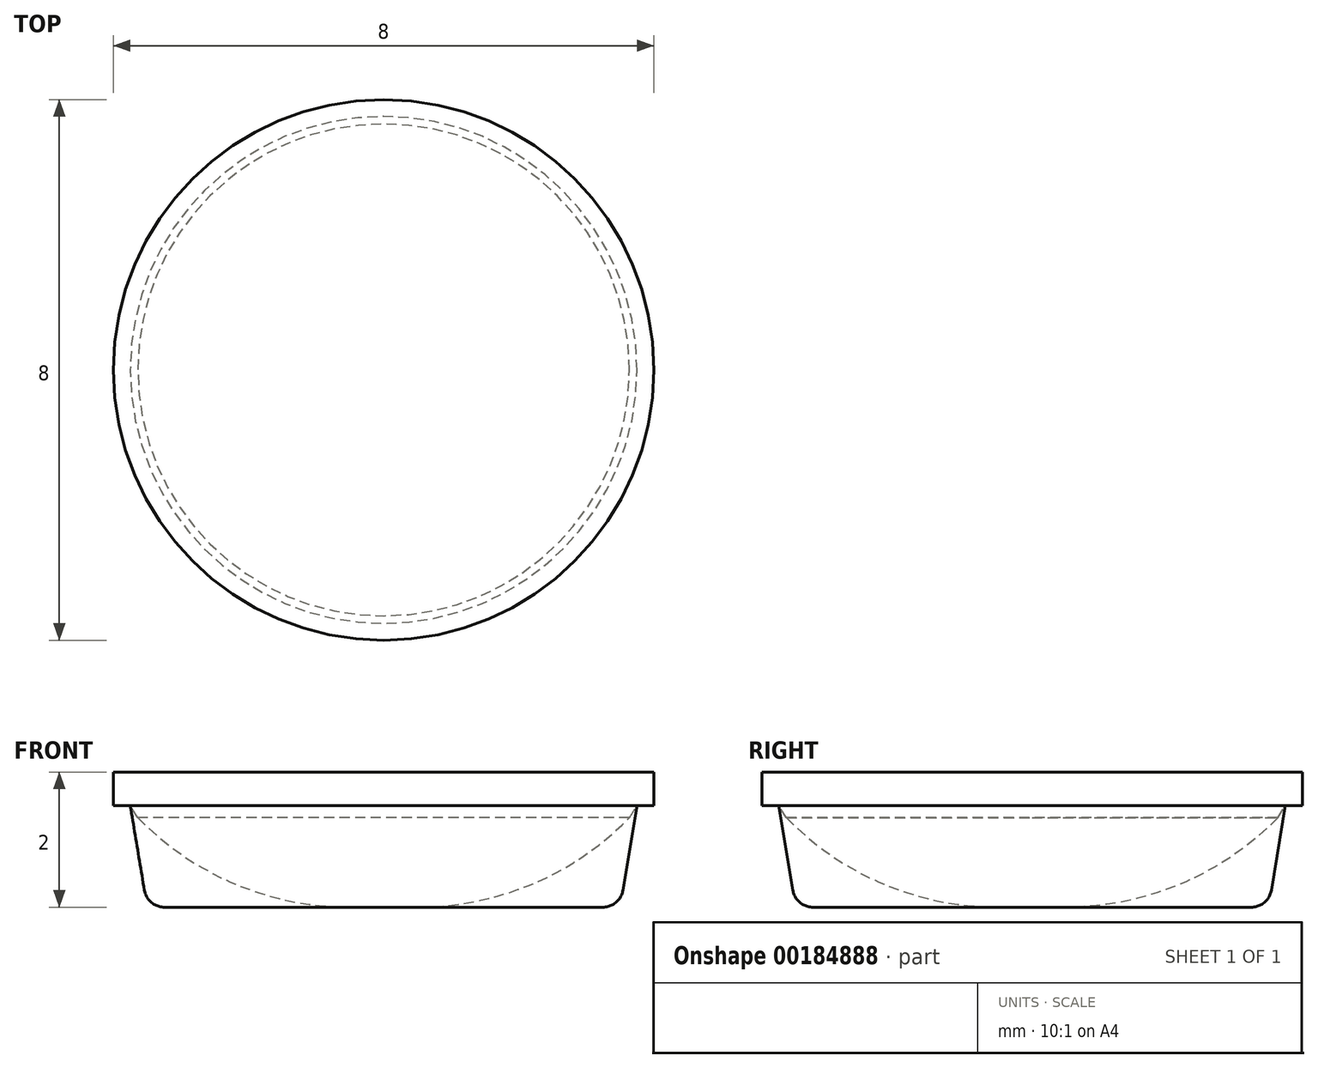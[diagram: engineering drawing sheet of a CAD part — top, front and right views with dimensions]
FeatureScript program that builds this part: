
annotation { "Feature Type Name" : "Feature", "Feature Type Description" : "" }
export const myFeature = defineFeature(function(context is Context, id is Id, definition is map)
    precondition{}
    {
        {
            var Q0;
            Q0=qCreatedBy(makeId("Top.planeOp"),FACE);
            cPlane(context, id + "F0", {"entities" : qUnion([Q0]), "cplaneType" : CPlaneType.OFFSET, "offset" : 2 * mm, "width" : 150 * mm, "height" : 150 * mm});
        }
        {
            var Q0;
            Q0=qCreatedBy(makeId("Front.planeOp"),FACE);
            var sketch = newSketch(context, id + "F1", { "sketchPlane" : qUnion([Q0])});
            skLineSegment(sketch, "E0", {"start": v(0, 0) * mm, "end": v(4, 0) * mm});
            skLineSegment(sketch, "E1", {"start": v(4, 0) * mm, "end": v(4, -0.5) * mm});
            skLineSegment(sketch, "E2", {"start": v(4, -0.5) * mm, "end": v(3.75, -0.5) * mm});
            skLineSegment(sketch, "E3", {"start": v(3.75, -0.5) * mm, "end": v(3.54, -1.75) * mm});
            skLineSegment(sketch, "E4", {"start": v(3.25, -2) * mm, "end": v(0, -2) * mm});
            skLineSegment(sketch, "E5", {"start": v(0, -2) * mm, "end": v(0, 0) * mm});
            skPoint(sketch, "E6.visualSharp", {"position": v(3.5, -2) * mm});
            skArc(sketch, "E6.filletArc", {"start": v(3.25, -2) * mm, "mid": v(3.44, -1.93) * mm, "end": v(3.54, -1.75) * mm});
            skSolve(sketch);
        }
        {
            var Q0;
            Q0=qSketchRegion(id+"F1",true);
            var Q1;
            Q1=sQuery(id+"F1.wireOp",EDGE,"E5");
            revolve(context, id + "F2", {"entities" : qUnion([Q0]), "axis" : qUnion([Q1]), "revolveType" : RevolveType.FULL});
        }
        {
            var Q0;
            Q0=qCreatedBy(makeId("Front.planeOp"),FACE);
            var sketch = newSketch(context, id + "F3", { "sketchPlane" : qUnion([Q0])});
            skLineSegment(sketch, "E7", {"start": v(0, 0) * mm, "end": v(4, 0) * mm});
            skLineSegment(sketch, "E8", {"start": v(4, 0) * mm, "end": v(4, -0.5) * mm});
            skLineSegment(sketch, "E9", {"start": v(4, -0.5) * mm, "end": v(3.75, -0.5) * mm});
            skLineSegment(sketch, "E10", {"start": v(3.75, -0.5) * mm, "end": v(3.64, -0.68) * mm});
            skLineSegment(sketch, "E11", {"start": v(0, 0) * mm, "end": v(0, -2) * mm});
            skLineSegment(sketch, "E12", {"start": v(0, -2) * mm, "end": v(0.5, -2) * mm});
            skArc(sketch, "E13", {"start": v(0.5, -2) * mm, "mid": v(2.2, -1.66) * mm, "end": v(3.64, -0.68) * mm});
            skSolve(sketch);
        }
        {
            var Q0;
            Q0=qSketchRegion(id+"F3",true);
            var Q1;
            Q1=sQuery(id+"F3.wireOp",EDGE,"E11");
            revolve(context, id + "F4", {"entities" : qUnion([Q0]), "axis" : qUnion([Q1]), "revolveType" : RevolveType.FULL});
        }
    });
